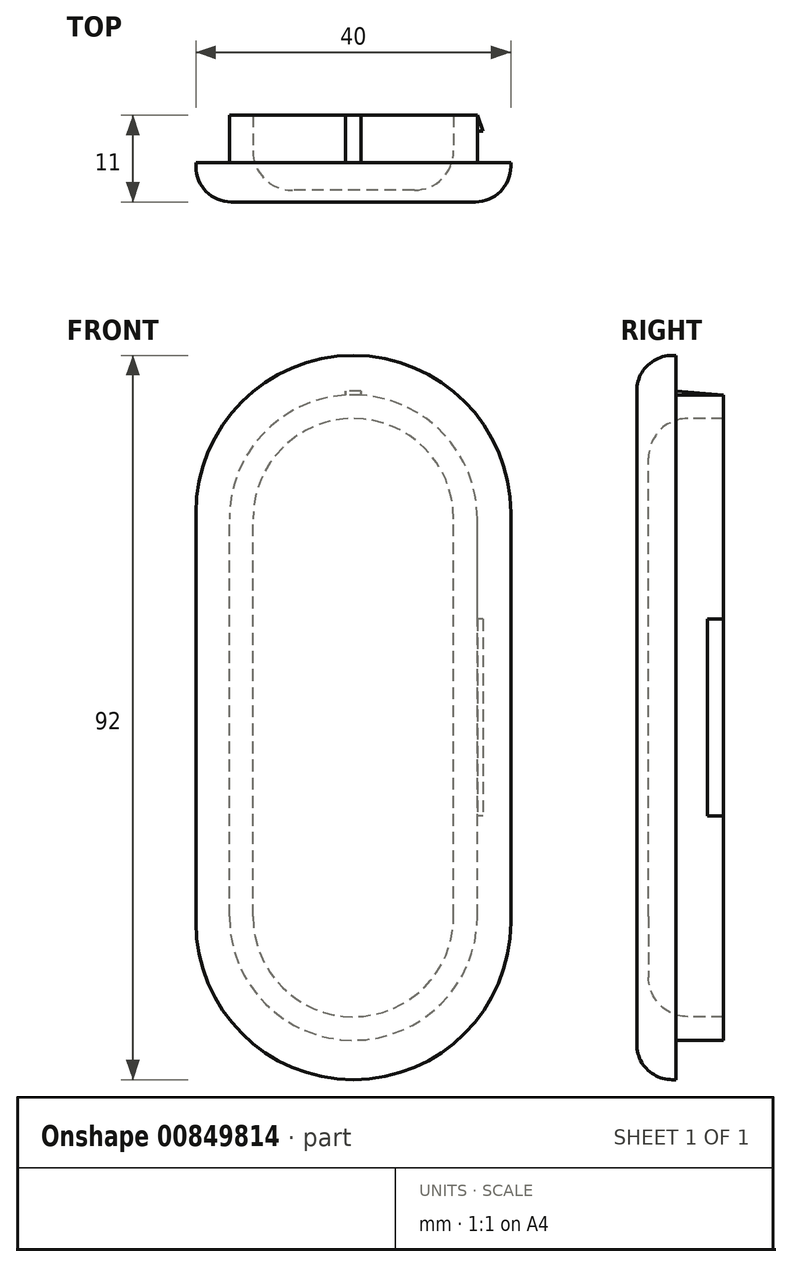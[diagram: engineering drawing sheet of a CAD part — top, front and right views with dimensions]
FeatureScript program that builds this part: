
annotation { "Feature Type Name" : "Feature", "Feature Type Description" : "" }
export const myFeature = defineFeature(function(context is Context, id is Id, definition is map)
    precondition{}
    {
        {
            var Q0;
            Q0=qCreatedBy(makeId("Front.planeOp"),FACE);
            var sketch = newSketch(context, id + "F0", { "sketchPlane" : qUnion([Q0])});
            skLineSegment(sketch, "E0.bottom", {"start": v(20, -46) * mm, "end": v(-20, -46) * mm});
            skLineSegment(sketch, "E0.top", {"start": v(20, 46) * mm, "end": v(-20, 46) * mm});
            skLineSegment(sketch, "E0.left", {"start": v(20, -46) * mm, "end": v(20, 46) * mm});
            skLineSegment(sketch, "E0.right", {"start": v(-20, -46) * mm, "end": v(-20, 46) * mm});
            skPoint(sketch, "E0.middle", {"position": v(0, 0) * mm});
            skSolve(sketch);
        }
        {
            var Q0;
            Q0=qSketchRegion(id+"F0",true);
            extrude(context, id + "F1", {"entities" : qUnion([Q0]), "depth" : 5 * mm, "offsetDistance" : 25 * mm});
        }
        {
            var Q0;
            Q0=makeQuery(id+"F1.opExtrude","SWEPT_EDGE",EDGE,{"disambiguationData":[OSD([sQuery(id+"F0.wireOp",EDGE,"E0.top"),sQuery(id+"F0.wireOp",EDGE,"E0.right")])]});
            var Q1;
            Q1=makeQuery(id+"F1.opExtrude","SWEPT_EDGE",EDGE,{"disambiguationData":[OSD([sQuery(id+"F0.wireOp",EDGE,"E0.top"),sQuery(id+"F0.wireOp",EDGE,"E0.left")])]});
            var Q2;
            Q2=makeQuery(id+"F1.opExtrude","SWEPT_EDGE",EDGE,{"disambiguationData":[OSD([sQuery(id+"F0.wireOp",EDGE,"E0.bottom"),sQuery(id+"F0.wireOp",EDGE,"E0.left")])]});
            var Q3;
            Q3=makeQuery(id+"F1.opExtrude","SWEPT_EDGE",EDGE,{"disambiguationData":[OSD([sQuery(id+"F0.wireOp",EDGE,"E0.bottom"),sQuery(id+"F0.wireOp",EDGE,"E0.right")])]});
            fillet(context, id + "F2", {"entities" : qUnion([Q0, Q1, Q2, Q3]), "radius" : 20 * mm, "tangentPropagation" : true, "allowEdgeOverflow" : false});
        }
        {
            var Q0;
            Q0=makeQuery(id+"F1.opExtrude","CAP_EDGE",EDGE,{"disambiguationData":[OSD([sQuery(id+"F0.wireOp",EDGE,"E0.left")])],"isStart":false});
            fillet(context, id + "F3", {"entities" : qUnion([Q0]), "radius" : 4.5 * mm, "tangentPropagation" : true, "allowEdgeOverflow" : false});
        }
        {
            var Q0;
            Q0=makeQuery(id+"F1.opExtrude","CAP_FACE",FACE,{"disambiguationData":[OSD([sQuery(id+"F0.wireOp",EDGE,"E0.bottom"),sQuery(id+"F0.wireOp",EDGE,"E0.top"),sQuery(id+"F0.wireOp",EDGE,"E0.left"),sQuery(id+"F0.wireOp",EDGE,"E0.right")])],"isStart":true});
            var sketch = newSketch(context, id + "F4", { "sketchPlane" : qUnion([Q0])});
            skLineSegment(sketch, "E1.bottom", {"start": v(0, -41) * mm, "end": v(0, -41) * mm});
            skLineSegment(sketch, "E1.top", {"start": v(0, 41) * mm, "end": v(0, 41) * mm});
            skLineSegment(sketch, "E1.left", {"start": v(15.75, -25.25) * mm, "end": v(15.75, 25.25) * mm});
            skLineSegment(sketch, "E1.right", {"start": v(-15.75, -25.25) * mm, "end": v(-15.75, 25.25) * mm});
            skPoint(sketch, "E1.middle", {"position": v(0, 0) * mm});
            skPoint(sketch, "E2.visualSharp", {"position": v(-15.75, 41) * mm});
            skArc(sketch, "E2.filletArc", {"start": v(0, 41) * mm, "mid": v(-11.14, 36.39) * mm, "end": v(-15.75, 25.25) * mm});
            skPoint(sketch, "E3.visualSharp", {"position": v(15.75, 41) * mm});
            skArc(sketch, "E3.filletArc", {"start": v(15.75, 25.25) * mm, "mid": v(11.14, 36.39) * mm, "end": v(0, 41) * mm});
            skPoint(sketch, "E4.visualSharp", {"position": v(-15.75, -41) * mm});
            skArc(sketch, "E4.filletArc", {"start": v(-15.75, -25.25) * mm, "mid": v(-11.14, -36.39) * mm, "end": v(0, -41) * mm});
            skPoint(sketch, "E5.visualSharp", {"position": v(15.75, -41) * mm});
            skArc(sketch, "E5.filletArc", {"start": v(0, -41) * mm, "mid": v(11.14, -36.39) * mm, "end": v(15.75, -25.25) * mm});
            skArc(sketch, "E6.0", {"start": v(0, -38) * mm, "mid": v(9.02, -34.27) * mm, "end": v(12.75, -25.25) * mm});
            skArc(sketch, "E6.1", {"start": v(12.75, 25.25) * mm, "mid": v(9.02, 34.27) * mm, "end": v(0, 38) * mm});
            skArc(sketch, "E6.2", {"start": v(0, 38) * mm, "mid": v(-9.02, 34.27) * mm, "end": v(-12.75, 25.25) * mm});
            skLineSegment(sketch, "E6.3", {"start": v(12.75, -25.25) * mm, "end": v(12.75, 25.25) * mm});
            skLineSegment(sketch, "E6.4", {"start": v(-12.75, -25.25) * mm, "end": v(-12.75, 25.25) * mm});
            skArc(sketch, "E6.5", {"start": v(-12.75, -25.25) * mm, "mid": v(-9.02, -34.27) * mm, "end": v(0, -38) * mm});
            skSolve(sketch);
        }
        {
            var Q0;
            Q0=qSketchRegion(id+"F4",true);
            extrude(context, id + "F5", {"entities" : qUnion([Q0]), "operationType" : NewBodyOperationType.ADD, "depth" : 6 * mm, "offsetDistance" : 25 * mm});
        }
        {
            var Q0;
            Q0=qCreatedBy(makeId("Top.planeOp"),FACE);
            var sketch = newSketch(context, id + "F6", { "sketchPlane" : qUnion([Q0])});
            skLineSegment(sketch, "E7.0.1", {"start": v(-15.75, 6) * mm, "end": v(15.75, 6) * mm});
            skLineSegment(sketch, "E7.0.3", {"start": v(-15.75, 6) * mm, "end": v(15.75, 6) * mm});
            skLineSegment(sketch, "E8", {"start": v(15.75, 6) * mm, "end": v(15.75, 4) * mm});
            skLineSegment(sketch, "E9", {"start": v(15.75, 4) * mm, "end": v(16.5, 4) * mm});
            skLineSegment(sketch, "E10", {"start": v(16.5, 4) * mm, "end": v(15.75, 6) * mm});
            skSolve(sketch);
        }
        {
            var Q0;
            Q0 = qSketchRegion(id + "F6", true);
            extrude(context, id + "F7", {"entities" : qUnion([Q0]), "operationType" : NewBodyOperationType.ADD, "endBound" : BoundingType.SYMMETRIC, "depth" : 25 * mm, "offsetDistance" : 25 * mm});
        }
        {
            var Q0;
            Q0=qCreatedBy(makeId("Right.planeOp"),FACE);
            var sketch = newSketch(context, id + "F8", { "sketchPlane" : qUnion([Q0])});
            skLineSegment(sketch, "E11.0.0", {"start": v(6, -12.5) * mm, "end": v(6, -25.25) * mm});
            skLineSegment(sketch, "E11.0.1", {"start": v(6, -25.25) * mm, "end": v(6, -41) * mm});
            skLineSegment(sketch, "E11.0.2", {"start": v(6, -25.25) * mm, "end": v(6, -12.5) * mm});
            skLineSegment(sketch, "E11.0.3", {"start": v(6, -12.5) * mm, "end": v(6, 12.5) * mm});
            skLineSegment(sketch, "E11.0.4", {"start": v(6, 12.5) * mm, "end": v(6, 25.25) * mm});
            skLineSegment(sketch, "E11.0.5", {"start": v(6, 25.25) * mm, "end": v(6, 41) * mm});
            skLineSegment(sketch, "E11.0.6", {"start": v(6, 25.25) * mm, "end": v(6, 12.5) * mm});
            skLineSegment(sketch, "E11.0.7", {"start": v(6, 12.5) * mm, "end": v(6, -12.5) * mm});
            skLineSegment(sketch, "E12", {"start": v(0, 41) * mm, "end": v(0, 41.5) * mm});
            skLineSegment(sketch, "E13", {"start": v(0, 41.5) * mm, "end": v(6, 41) * mm});
            skLineSegment(sketch, "E14", {"start": v(6, 41) * mm, "end": v(6, 40) * mm});
            skLineSegment(sketch, "E15", {"start": v(6, 40) * mm, "end": v(0, 40) * mm});
            skLineSegment(sketch, "E16", {"start": v(0, 40) * mm, "end": v(0, 41) * mm});
            skSolve(sketch);
        }
        {
            var Q0;
            Q0=makeQuery(id+"F8.imprint","IMPRINT",FACE,{"disambiguationData":[TD([[makeQuery(id+"F8.imprint","IMPRINT",EDGE,{"derivedFrom":sQuery(id+"F8.wireOp",EDGE,"E12")}),-1.0]])]});
            extrude(context, id + "F9", {"entities" : qUnion([Q0]), "operationType" : NewBodyOperationType.ADD, "endBound" : BoundingType.SYMMETRIC, "depth" : 2 * mm, "offsetDistance" : 25 * mm});
        }
        {
            var Q0;
            Q0=makeQuery(id+"F5.boolean.opBoolean","SPLIT",FACE,{"disambiguationData":[TD([makeQuery(id+"F5.opExtrude","SWEPT_FACE",FACE,{"disambiguationData":[OSD([sQuery(id+"F4.wireOp",EDGE,"E6.3")])]})])],"derivedFrom":makeQuery(id+"F1.opExtrude","CAP_FACE",FACE,{"disambiguationData":[OSD([sQuery(id+"F0.wireOp",EDGE,"E0.bottom"),sQuery(id+"F0.wireOp",EDGE,"E0.top"),sQuery(id+"F0.wireOp",EDGE,"E0.left"),sQuery(id+"F0.wireOp",EDGE,"E0.right")])],"isStart":true})});
            extrude(context, id + "F10", {"entities" : qUnion([Q0]), "operationType" : NewBodyOperationType.REMOVE, "oppositeDirection" : true, "depth" : 3.5 * mm, "offsetDistance" : 25 * mm});
        }
        {
            var Q0;
            Q0=makeQuery(id+"F10.boolean.opBoolean","COPY",FACE,{"derivedFrom":makeQuery(id+"F10.opExtrude","CAP_FACE",FACE,{"disambiguationData":[OSD([sQuery(id+"F0.wireOp",EDGE,"E0.bottom"),sQuery(id+"F0.wireOp",EDGE,"E0.top"),sQuery(id+"F0.wireOp",EDGE,"E0.left"),sQuery(id+"F0.wireOp",EDGE,"E0.right")])],"isStart":false})});
            fillet(context, id + "F11", {"entities" : qUnion([Q0]), "radius" : 5 * mm, "tangentPropagation" : true, "allowEdgeOverflow" : false});
        }
    });
